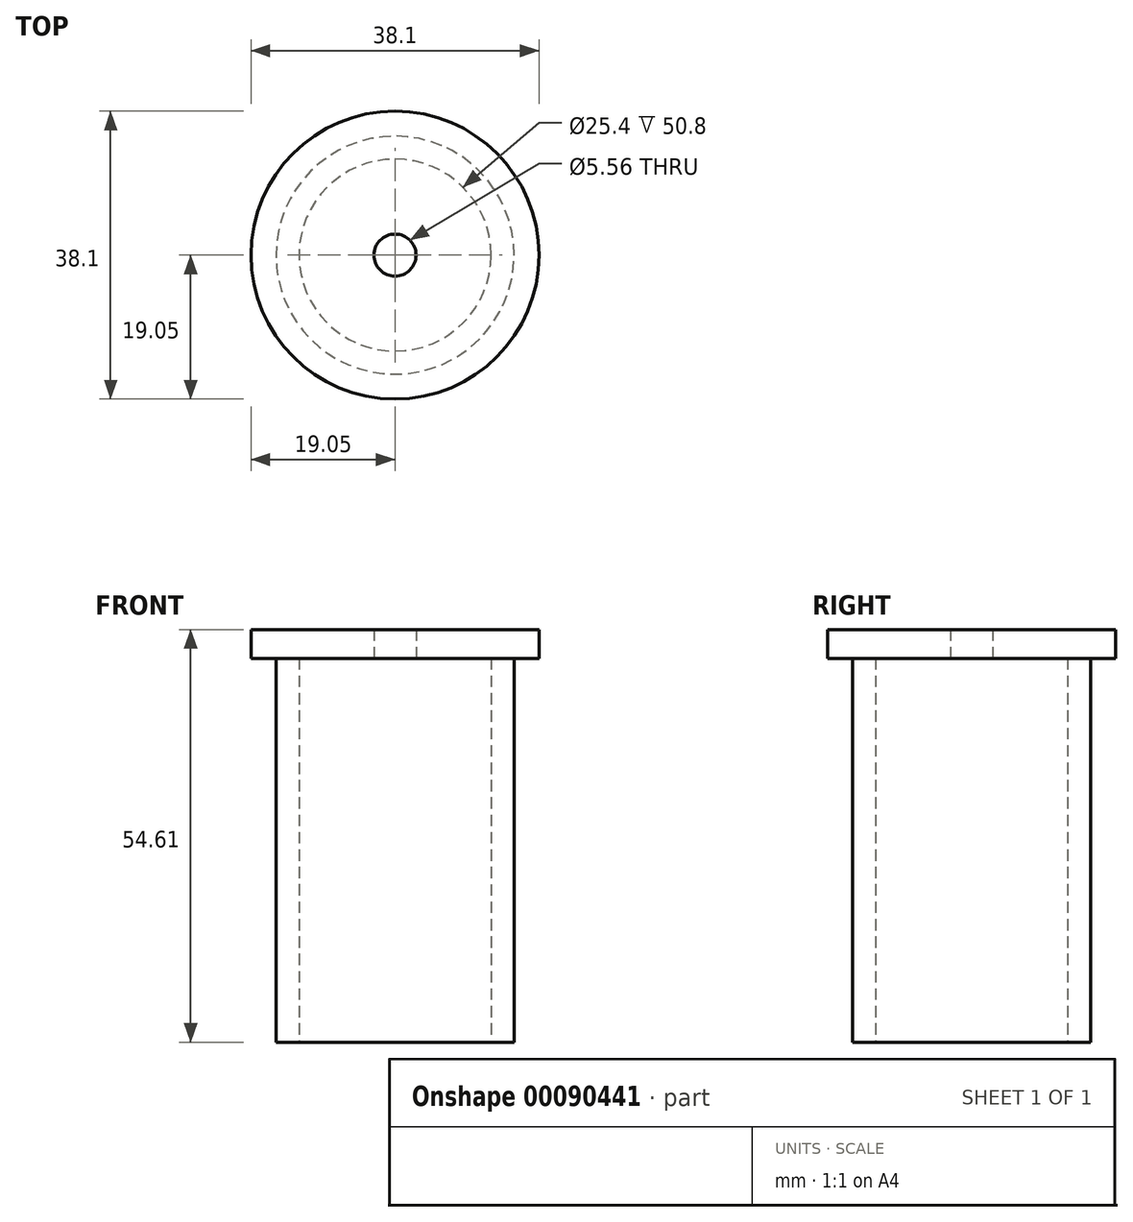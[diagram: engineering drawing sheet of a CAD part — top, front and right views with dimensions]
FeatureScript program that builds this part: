
annotation { "Feature Type Name" : "Feature", "Feature Type Description" : "" }
export const myFeature = defineFeature(function(context is Context, id is Id, definition is map)
    precondition{}
    {
        {
            var Q0;
            Q0=qCreatedBy(makeId("Top.planeOp"),FACE);
            var sketch = newSketch(context, id + "F0", { "sketchPlane" : qUnion([Q0])});
            skCircle(sketch, "E0", {"center": v(0, 0) * mm, "radius": 15.75 * mm});
            skCircle(sketch, "E1", {"center": v(0, 0) * mm, "radius": 12.7 * mm});
            skSolve(sketch);
        }
        {
            var Q0;
            Q0 = qSketchRegion(id + "F0", true);
            extrude(context, id + "F1", {"entities" : qUnion([Q0]), "depth" : 50.8 * mm});
        }
        {
            var Q0;
            Q0=makeQuery(id+"F1.opExtrude","CAP_FACE",FACE,{"disambiguationData":[OSD([sQuery(id+"F0.wireOp",EDGE,"E0"),sQuery(id+"F0.wireOp",EDGE,"E1")])],"isStart":false});
            var sketch = newSketch(context, id + "F2", { "sketchPlane" : qUnion([Q0])});
            skCircle(sketch, "E2", {"center": v(0, 0) * mm, "radius": 19.05 * mm});
            skSolve(sketch);
        }
        {
            var Q0;
            Q0 = qSketchRegion(id + "F2", true);
            extrude(context, id + "F3", {"entities" : qUnion([Q0]), "operationType" : NewBodyOperationType.ADD, "depth" : 3.8 * mm});
        }
        {
            var Q0;
            Q0=sQuery(id+"F2.wireOp",VERTEX,"E2.center");
            var Q1;
            Q1=makeQuery(id+"F1.opExtrude","SWEPT_BODY",BODY,{"disambiguationData":[OSD([sQuery(id+"F0.wireOp",EDGE,"E0"),sQuery(id+"F0.wireOp",EDGE,"E1")])]});
            hole(context, id + "F4", {"style" : HoleStyle.SIMPLE, "endStyle" : HoleEndStyle.THROUGH, "oppositeDirection" : true, "holeDiameter" : 5.56 * mm, "locations" : qUnion([Q0]), "scope" : qUnion([Q1]), "isTappedThrough" : true});
        }
    });
